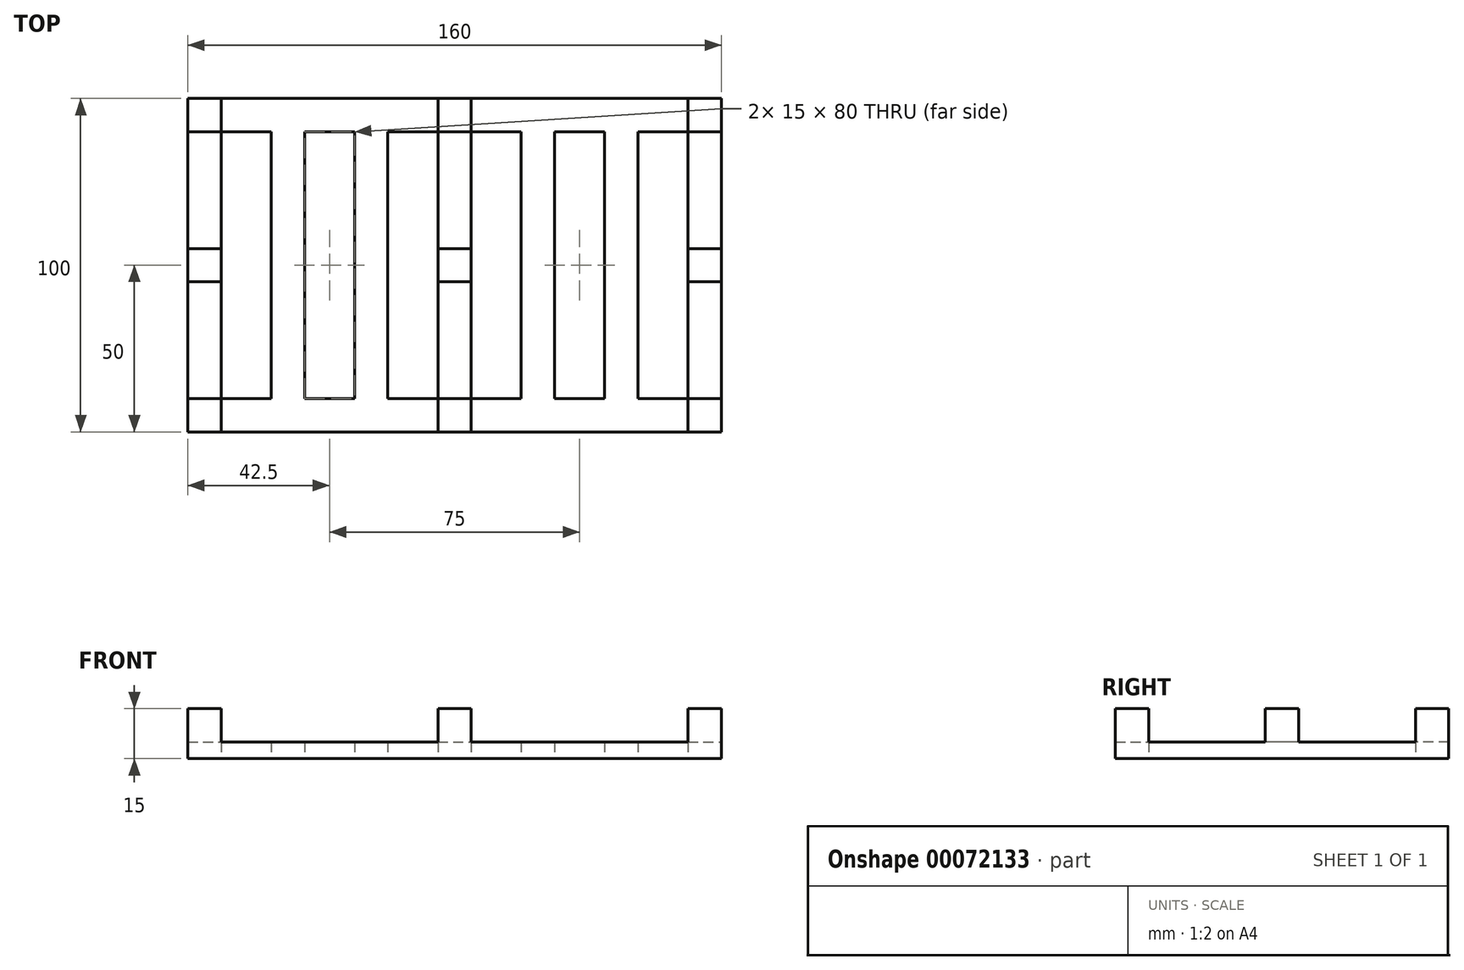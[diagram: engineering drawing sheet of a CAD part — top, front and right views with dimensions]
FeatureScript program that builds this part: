
annotation { "Feature Type Name" : "Feature", "Feature Type Description" : "" }
export const myFeature = defineFeature(function(context is Context, id is Id, definition is map)
    precondition{}
    {
        {
            var Q0;
            Q0=qCreatedBy(makeId("Top.planeOp"),FACE);
            var sketch = newSketch(context, id + "F0", { "sketchPlane" : qUnion([Q0])});
            skLineSegment(sketch, "E0.bottom", {"start": v(0, 0) * mm, "end": v(160, 0) * mm});
            skLineSegment(sketch, "E0.top", {"start": v(0, 100) * mm, "end": v(160, 100) * mm});
            skLineSegment(sketch, "E0.left", {"start": v(0, 0) * mm, "end": v(0, 100) * mm});
            skLineSegment(sketch, "E0.right", {"start": v(160, 0) * mm, "end": v(160, 100) * mm});
            skLineSegment(sketch, "E1.0", {"start": v(150, 10) * mm, "end": v(150, 90) * mm});
            skLineSegment(sketch, "E1.1", {"start": v(10, 10) * mm, "end": v(25, 10) * mm});
            skLineSegment(sketch, "E1.2", {"start": v(10, 10) * mm, "end": v(10, 90) * mm});
            skLineSegment(sketch, "E1.3", {"start": v(10, 90) * mm, "end": v(25, 90) * mm});
            skLineSegment(sketch, "E2", {"start": v(80, 90) * mm, "end": v(80, 10) * mm, "construction": true});
            skPoint(sketch, "E2.endSnap0", {"position": v(80, 10) * mm});
            skLineSegment(sketch, "E3.0", {"start": v(75, 90) * mm, "end": v(75, 10) * mm});
            skLineSegment(sketch, "E4.0", {"start": v(85, 90) * mm, "end": v(85, 10) * mm});
            skLineSegment(sketch, "E5.1.0.0", {"start": v(110, 90) * mm, "end": v(110, 10) * mm});
            skLineSegment(sketch, "E5.1.0.1", {"start": v(100, 90) * mm, "end": v(100, 10) * mm});
            skLineSegment(sketch, "E5.2.0.0", {"start": v(135, 90) * mm, "end": v(135, 10) * mm});
            skLineSegment(sketch, "E5.2.0.1", {"start": v(125, 90) * mm, "end": v(125, 10) * mm});
            skLineSegment(sketch, "E5.direction1", {"start": v(85, 10) * mm, "end": v(110, 10) * mm, "construction": true});
            skLineSegment(sketch, "E6.1.0.0", {"start": v(60, 90) * mm, "end": v(60, 10) * mm});
            skLineSegment(sketch, "E6.1.0.1", {"start": v(50, 90) * mm, "end": v(50, 10) * mm});
            skLineSegment(sketch, "E6.2.0.0", {"start": v(35, 90) * mm, "end": v(35, 10) * mm});
            skLineSegment(sketch, "E6.2.0.1", {"start": v(25, 90) * mm, "end": v(25, 10) * mm});
            skLineSegment(sketch, "E6.direction1", {"start": v(85, 10) * mm, "end": v(60, 10) * mm, "construction": true});
            skLineSegment(sketch, "E7.trimOffspring", {"start": v(35, 90) * mm, "end": v(50, 90) * mm});
            skLineSegment(sketch, "E8.trimOffspring", {"start": v(60, 90) * mm, "end": v(75, 90) * mm});
            skLineSegment(sketch, "E9.trimOffspring", {"start": v(85, 90) * mm, "end": v(100, 90) * mm});
            skLineSegment(sketch, "E10.trimOffspring", {"start": v(110, 90) * mm, "end": v(125, 90) * mm});
            skLineSegment(sketch, "E11.trimOffspring", {"start": v(135, 90) * mm, "end": v(150, 90) * mm});
            skLineSegment(sketch, "E12.trimOffspring", {"start": v(135, 10) * mm, "end": v(150, 10) * mm});
            skLineSegment(sketch, "E13.trimOffspring", {"start": v(110, 10) * mm, "end": v(125, 10) * mm});
            skLineSegment(sketch, "E14.trimOffspring", {"start": v(85, 10) * mm, "end": v(100, 10) * mm});
            skLineSegment(sketch, "E15.trimOffspring", {"start": v(60, 10) * mm, "end": v(75, 10) * mm});
            skLineSegment(sketch, "E16.trimOffspring", {"start": v(35, 10) * mm, "end": v(50, 10) * mm});
            skSolve(sketch);
        }
        {
            var Q0;
            Q0=makeQuery(id+"F0.imprint","IMPRINT",FACE,{"disambiguationData":[TD([[makeQuery(id+"F0.imprint","IMPRINT",EDGE,{"derivedFrom":sQuery(id+"F0.wireOp",EDGE,"E0.bottom")}),1.0]])]});
            extrude(context, id + "F1", {"entities" : qUnion([Q0]), "depth" : 5 * mm});
        }
        {
            var Q0;
            Q0=makeQuery(id+"F1.opExtrude","CAP_FACE",FACE,{"disambiguationData":[OSD([sQuery(id+"F0.wireOp",EDGE,"E0.bottom"),sQuery(id+"F0.wireOp",EDGE,"E0.top"),sQuery(id+"F0.wireOp",EDGE,"E0.left"),sQuery(id+"F0.wireOp",EDGE,"E0.right"),sQuery(id+"F0.wireOp",EDGE,"E1.0"),sQuery(id+"F0.wireOp",EDGE,"E1.1"),sQuery(id+"F0.wireOp",EDGE,"E1.2"),sQuery(id+"F0.wireOp",EDGE,"E1.3"),sQuery(id+"F0.wireOp",EDGE,"E3.0"),sQuery(id+"F0.wireOp",EDGE,"E4.0"),sQuery(id+"F0.wireOp",EDGE,"E5.1.0.0"),sQuery(id+"F0.wireOp",EDGE,"E5.1.0.1"),sQuery(id+"F0.wireOp",EDGE,"E5.2.0.0"),sQuery(id+"F0.wireOp",EDGE,"E5.2.0.1"),sQuery(id+"F0.wireOp",EDGE,"E6.1.0.0"),sQuery(id+"F0.wireOp",EDGE,"E6.1.0.1"),sQuery(id+"F0.wireOp",EDGE,"E6.2.0.0"),sQuery(id+"F0.wireOp",EDGE,"E6.2.0.1"),sQuery(id+"F0.wireOp",EDGE,"E7.trimOffspring"),sQuery(id+"F0.wireOp",EDGE,"E8.trimOffspring"),sQuery(id+"F0.wireOp",EDGE,"E9.trimOffspring"),sQuery(id+"F0.wireOp",EDGE,"E10.trimOffspring"),sQuery(id+"F0.wireOp",EDGE,"E11.trimOffspring"),sQuery(id+"F0.wireOp",EDGE,"E12.trimOffspring"),sQuery(id+"F0.wireOp",EDGE,"E13.trimOffspring"),sQuery(id+"F0.wireOp",EDGE,"E14.trimOffspring"),sQuery(id+"F0.wireOp",EDGE,"E15.trimOffspring"),sQuery(id+"F0.wireOp",EDGE,"E16.trimOffspring")])],"isStart":false});
            var sketch = newSketch(context, id + "F2", { "sketchPlane" : qUnion([Q0])});
            skLineSegment(sketch, "E17", {"start": v(0, 50) * mm, "end": v(10, 50) * mm, "construction": true});
            skLineSegment(sketch, "E18.0", {"start": v(0, 45) * mm, "end": v(10, 45) * mm});
            skLineSegment(sketch, "E19.0", {"start": v(0, 55) * mm, "end": v(10, 55) * mm});
            skLineSegment(sketch, "E20", {"start": v(0, 55) * mm, "end": v(0, 45) * mm});
            skLineSegment(sketch, "E21", {"start": v(10, 45) * mm, "end": v(10, 55) * mm});
            skLineSegment(sketch, "E22.direction1", {"start": v(10, 45) * mm, "end": v(85, 45) * mm, "construction": true});
            skLineSegment(sketch, "E23.0.1.0", {"start": v(85, 45) * mm, "end": v(85, 55) * mm});
            skLineSegment(sketch, "E23.3.1.0", {"start": v(75, 55) * mm, "end": v(85, 55) * mm});
            skLineSegment(sketch, "E23.6.1.0", {"start": v(75, 55) * mm, "end": v(75, 45) * mm});
            skLineSegment(sketch, "E23.9.1.0", {"start": v(75, 45) * mm, "end": v(85, 45) * mm});
            skLineSegment(sketch, "E23.0.2.0", {"start": v(160, 45) * mm, "end": v(160, 55) * mm});
            skLineSegment(sketch, "E23.3.2.0", {"start": v(150, 55) * mm, "end": v(160, 55) * mm});
            skLineSegment(sketch, "E23.6.2.0", {"start": v(150, 55) * mm, "end": v(150, 45) * mm});
            skLineSegment(sketch, "E23.9.2.0", {"start": v(150, 45) * mm, "end": v(160, 45) * mm});
            skLineSegment(sketch, "E24.0.1.0", {"start": v(0, 90) * mm, "end": v(10, 90) * mm});
            skLineSegment(sketch, "E24.0.1.1", {"start": v(0, 100) * mm, "end": v(10, 100) * mm});
            skLineSegment(sketch, "E24.0.1.2", {"start": v(85, 90) * mm, "end": v(85, 100) * mm});
            skLineSegment(sketch, "E24.0.1.3", {"start": v(150, 90) * mm, "end": v(160, 90) * mm});
            skLineSegment(sketch, "E24.0.1.4", {"start": v(150, 100) * mm, "end": v(150, 90) * mm});
            skLineSegment(sketch, "E24.0.1.5", {"start": v(150, 100) * mm, "end": v(160, 100) * mm});
            skLineSegment(sketch, "E24.0.1.6", {"start": v(160, 90) * mm, "end": v(160, 100) * mm});
            skLineSegment(sketch, "E24.0.1.7", {"start": v(75, 90) * mm, "end": v(85, 90) * mm});
            skLineSegment(sketch, "E24.0.1.8", {"start": v(75, 100) * mm, "end": v(75, 90) * mm});
            skLineSegment(sketch, "E24.0.1.9", {"start": v(75, 100) * mm, "end": v(85, 100) * mm});
            skLineSegment(sketch, "E24.0.1.10", {"start": v(0, 100) * mm, "end": v(0, 90) * mm});
            skLineSegment(sketch, "E24.0.1.11", {"start": v(10, 90) * mm, "end": v(10, 100) * mm});
            skLineSegment(sketch, "E24.direction1", {"start": v(0, 45) * mm, "end": v(25, 45) * mm, "construction": true});
            skLineSegment(sketch, "E24.direction2", {"start": v(0, 45) * mm, "end": v(0, 90) * mm, "construction": true});
            skLineSegment(sketch, "E25.0.1.0", {"start": v(150, 10) * mm, "end": v(160, 10) * mm});
            skLineSegment(sketch, "E25.0.1.1", {"start": v(150, 10) * mm, "end": v(150, 0) * mm});
            skLineSegment(sketch, "E25.0.1.2", {"start": v(75, 10) * mm, "end": v(75, 0) * mm});
            skLineSegment(sketch, "E25.0.1.3", {"start": v(10, 0) * mm, "end": v(10, 10) * mm});
            skLineSegment(sketch, "E25.0.1.4", {"start": v(0, 10) * mm, "end": v(10, 10) * mm});
            skLineSegment(sketch, "E25.0.1.5", {"start": v(0, 0) * mm, "end": v(10, 0) * mm});
            skLineSegment(sketch, "E25.0.1.6", {"start": v(150, 0) * mm, "end": v(160, 0) * mm});
            skLineSegment(sketch, "E25.0.1.7", {"start": v(75, 0) * mm, "end": v(85, 0) * mm});
            skLineSegment(sketch, "E25.0.1.8", {"start": v(0, 10) * mm, "end": v(0, 0) * mm});
            skLineSegment(sketch, "E25.0.1.9", {"start": v(85, 0) * mm, "end": v(85, 10) * mm});
            skLineSegment(sketch, "E25.0.1.10", {"start": v(160, 0) * mm, "end": v(160, 10) * mm});
            skLineSegment(sketch, "E25.0.1.11", {"start": v(75, 10) * mm, "end": v(85, 10) * mm});
            skLineSegment(sketch, "E25.0.1.12", {"start": v(0, -45) * mm, "end": v(0, 0) * mm, "construction": true});
            skLineSegment(sketch, "E25.direction1", {"start": v(150, 100) * mm, "end": v(175, 100) * mm, "construction": true});
            skLineSegment(sketch, "E25.direction2", {"start": v(150, 100) * mm, "end": v(150, 10) * mm, "construction": true});
            skSolve(sketch);
        }
        {
            var Q0;
            Q0=makeQuery(id+"F2.imprint","IMPRINT",FACE,{"disambiguationData":[TD([[makeQuery(id+"F2.imprint","IMPRINT",EDGE,{"derivedFrom":sQuery(id+"F2.wireOp",EDGE,"E24.0.1.0")}),1.0]])]});
            var Q1;
            Q1=makeQuery(id+"F2.imprint","IMPRINT",FACE,{"disambiguationData":[TD([[makeQuery(id+"F2.imprint","IMPRINT",EDGE,{"derivedFrom":sQuery(id+"F2.wireOp",EDGE,"E24.0.1.2")}),1.0]])]});
            var Q2;
            Q2=makeQuery(id+"F2.imprint","IMPRINT",FACE,{"disambiguationData":[TD([[makeQuery(id+"F2.imprint","IMPRINT",EDGE,{"derivedFrom":sQuery(id+"F2.wireOp",EDGE,"E24.0.1.3")}),1.0]])]});
            var Q3;
            Q3=makeQuery(id+"F2.imprint","IMPRINT",FACE,{"disambiguationData":[TD([[makeQuery(id+"F2.imprint","IMPRINT",EDGE,{"derivedFrom":sQuery(id+"F2.wireOp",EDGE,"E23.0.2.0")}),1.0]])]});
            var Q4;
            Q4=makeQuery(id+"F2.imprint","IMPRINT",FACE,{"disambiguationData":[TD([[makeQuery(id+"F2.imprint","IMPRINT",EDGE,{"derivedFrom":sQuery(id+"F2.wireOp",EDGE,"E23.0.1.0")}),-1.0]])]});
            var Q5;
            Q5=makeQuery(id+"F2.imprint","IMPRINT",FACE,{"disambiguationData":[TD([[makeQuery(id+"F2.imprint","IMPRINT",EDGE,{"derivedFrom":sQuery(id+"F2.wireOp",EDGE,"E18.0")}),1.0]])]});
            var Q6;
            Q6=makeQuery(id+"F2.imprint","IMPRINT",FACE,{"disambiguationData":[TD([[makeQuery(id+"F2.imprint","IMPRINT",EDGE,{"derivedFrom":sQuery(id+"F2.wireOp",EDGE,"E25.0.1.3")}),1.0]])]});
            var Q7;
            Q7=makeQuery(id+"F2.imprint","IMPRINT",FACE,{"disambiguationData":[TD([[makeQuery(id+"F2.imprint","IMPRINT",EDGE,{"derivedFrom":sQuery(id+"F2.wireOp",EDGE,"E25.0.1.0")}),-1.0]])]});
            var Q8;
            Q8=makeQuery(id+"F2.imprint","IMPRINT",FACE,{"disambiguationData":[TD([[makeQuery(id+"F2.imprint","IMPRINT",EDGE,{"derivedFrom":sQuery(id+"F2.wireOp",EDGE,"E25.0.1.2")}),1.0]])]});
            extrude(context, id + "F3", {"entities" : qUnion([Q0, Q1, Q2, Q3, Q4, Q5, Q6, Q7, Q8]), "operationType" : NewBodyOperationType.ADD, "depth" : 10 * mm});
        }
    });
